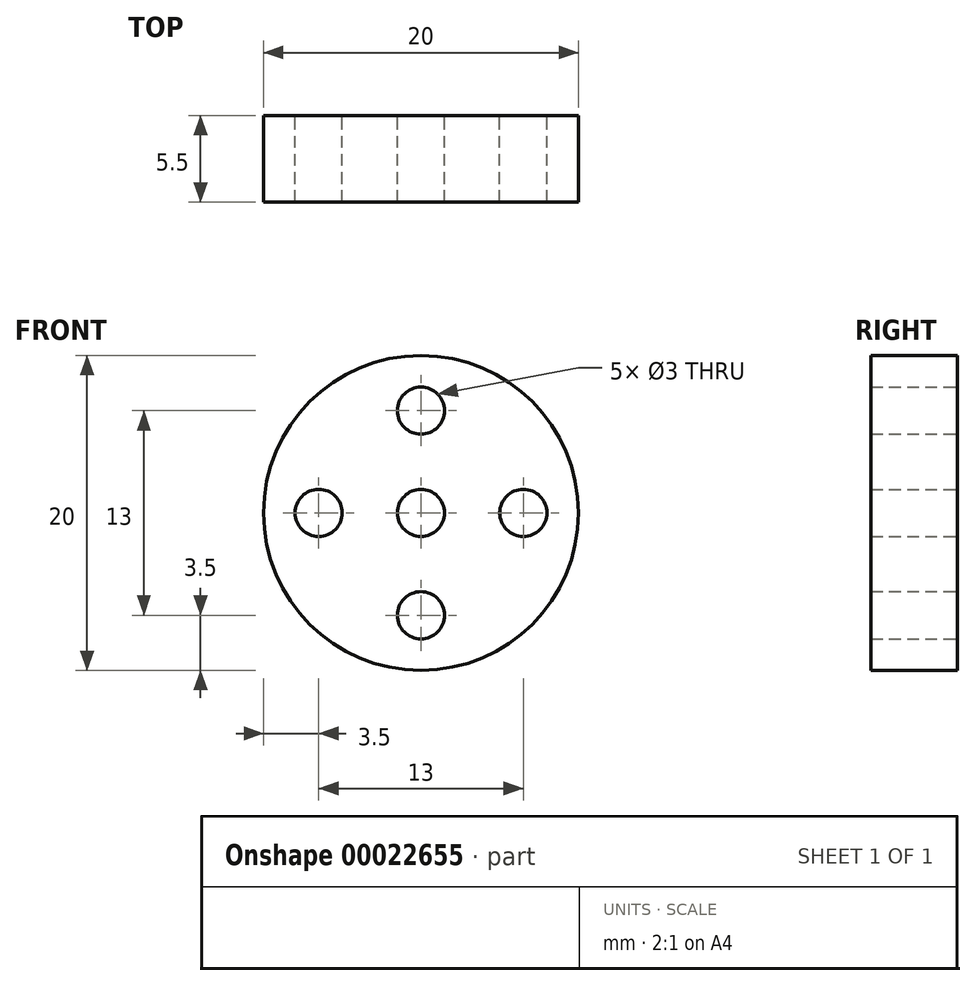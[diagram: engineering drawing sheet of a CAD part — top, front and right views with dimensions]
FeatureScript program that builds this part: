
annotation { "Feature Type Name" : "Feature", "Feature Type Description" : "" }
export const myFeature = defineFeature(function(context is Context, id is Id, definition is map)
    precondition{}
    {
        {
            var Q0;
            Q0=qCreatedBy(makeId("Front.planeOp"),FACE);
            var sketch = newSketch(context, id + "F0", { "sketchPlane" : qUnion([Q0])});
            skCircle(sketch, "E0", {"center": v(0, 0) * mm, "radius": 1.5 * mm});
            skCircle(sketch, "E1", {"center": v(0, 0) * mm, "radius": 5 * mm});
            skCircle(sketch, "E2", {"center": v(0, 0) * mm, "radius": 8 * mm});
            skCircle(sketch, "E3", {"center": v(0, 0) * mm, "radius": 10 * mm});
            skCircle(sketch, "E4", {"center": v(0, 6.5) * mm, "radius": 1.5 * mm});
            skCircle(sketch, "E5.1.0", {"center": v(-6.5, 0) * mm, "radius": 1.5 * mm});
            skCircle(sketch, "E5.2.0", {"center": v(0, -6.5) * mm, "radius": 1.5 * mm});
            skCircle(sketch, "E5.3.0", {"center": v(6.5, 0) * mm, "radius": 1.5 * mm});
            skSolve(sketch);
        }
        {
            var Q0;
            Q0=makeQuery(id+"F0.imprint","IMPRINT",FACE,{"disambiguationData":[TD([[makeQuery(id+"F0.imprint","IMPRINT",EDGE,{"derivedFrom":sQuery(id+"F0.wireOp",EDGE,"E0")}),-1.0]])]});
            var Q1;
            {var subQ3=sQuery(id+"F0.wireOp",EDGE,"E1");var subQ5=sQuery(id+"F0.wireOp",EDGE,"E4");var subQ7=makeQuery(id+"F0.imprint","INTERSECT",VERTEX,{"derivedFrom":[subQ3,subQ5]});Q1=makeQuery(id+"F0.imprint","IMPRINT",FACE,{"disambiguationData":[TD([[makeQuery(id+"F0.imprint","IMPRINT",EDGE,{"disambiguationData":[TD([[subQ7,-1.0]])],"derivedFrom":subQ3}),-1.0]])]});}
            var Q2;
            {var subQ3=sQuery(id+"F0.wireOp",EDGE,"E1");var subQ5=sQuery(id+"F0.wireOp",EDGE,"E5.1.0");var subQ7=makeQuery(id+"F0.imprint","INTERSECT",VERTEX,{"derivedFrom":[subQ3,subQ5]});Q2=makeQuery(id+"F0.imprint","IMPRINT",FACE,{"disambiguationData":[TD([[makeQuery(id+"F0.imprint","IMPRINT",EDGE,{"disambiguationData":[TD([[subQ7,-1.0]])],"derivedFrom":subQ3}),-1.0]])]});}
            var Q3;
            {var subQ0=sQuery(id+"F0.wireOp",EDGE,"E5.3.0");var subQ3=sQuery(id+"F0.wireOp",EDGE,"E1");var subQ4=makeQuery(id+"F0.imprint","INTERSECT",VERTEX,{"derivedFrom":[subQ3,subQ0]});Q3=makeQuery(id+"F0.imprint","IMPRINT",FACE,{"disambiguationData":[TD([[makeQuery(id+"F0.imprint","IMPRINT",EDGE,{"disambiguationData":[TD([[subQ4,1.0]])],"derivedFrom":subQ3}),-1.0]])]});}
            var Q4;
            {var subQ3=sQuery(id+"F0.wireOp",EDGE,"E1");var subQ5=sQuery(id+"F0.wireOp",EDGE,"E4");var subQ7=makeQuery(id+"F0.imprint","INTERSECT",VERTEX,{"derivedFrom":[subQ3,subQ5]});Q4=makeQuery(id+"F0.imprint","IMPRINT",FACE,{"disambiguationData":[TD([[makeQuery(id+"F0.imprint","IMPRINT",EDGE,{"disambiguationData":[TD([[subQ7,1.0]])],"derivedFrom":subQ3}),-1.0]])]});}
            var Q5;
            Q5=makeQuery(id+"F0.imprint","IMPRINT",FACE,{"disambiguationData":[TD([[makeQuery(id+"F0.imprint","IMPRINT",EDGE,{"derivedFrom":sQuery(id+"F0.wireOp",EDGE,"E3")}),1.0]])]});
            extrude(context, id + "F1", {"entities" : qUnion([Q0, Q1, Q2, Q3, Q4, Q5]), "endBound" : BoundingType.SYMMETRIC, "depth" : 5.5 * mm});
        }
    });
